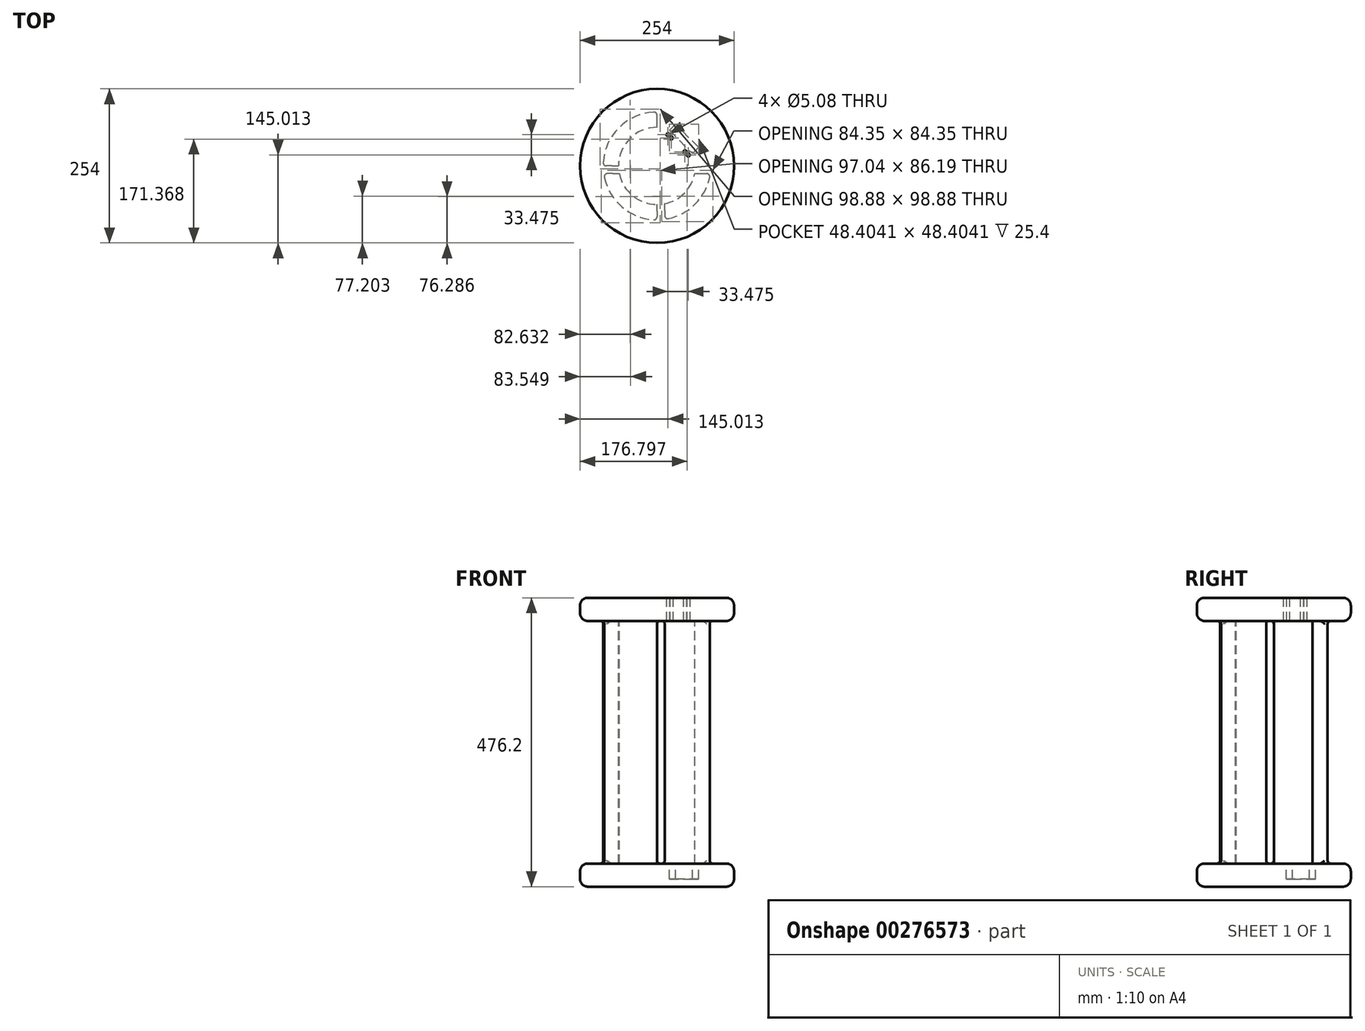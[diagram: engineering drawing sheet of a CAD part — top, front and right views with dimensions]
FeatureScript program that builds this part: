
annotation { "Feature Type Name" : "Feature", "Feature Type Description" : "" }
export const myFeature = defineFeature(function(context is Context, id is Id, definition is map)
    precondition{}
    {
        {
            var Q0;
            Q0=qCreatedBy(makeId("Top.planeOp"),FACE);
            var sketch = newSketch(context, id + "F0", { "sketchPlane" : qUnion([Q0])});
            skCircle(sketch, "E0", {"center": v(0, 0) * mm, "radius": 127 * mm});
            skSolve(sketch);
        }
        {
            var Q0;
            Q0 = qSketchRegion(id + "F0", true);
            extrude(context, id + "F1", {"entities" : qUnion([Q0]), "depth" : 38.1 * mm});
        }
        {
            var Q0;
            Q0=qCreatedBy(makeId("Front.planeOp"),FACE);
            var sketch = newSketch(context, id + "F2", { "sketchPlane" : qUnion([Q0])});
            skLineSegment(sketch, "E1.bottom", {"start": v(0, 0) * mm, "end": v(88.9, 0) * mm});
            skLineSegment(sketch, "E1.top", {"start": v(0, -400) * mm, "end": v(88.9, -400) * mm});
            skLineSegment(sketch, "E1.left", {"start": v(0, 0) * mm, "end": v(0, -400) * mm});
            skLineSegment(sketch, "E1.right", {"start": v(88.9, 0) * mm, "end": v(88.9, -400) * mm});
            skLineSegment(sketch, "E2", {"start": v(88.9, -200) * mm, "end": v(0, -200) * mm, "construction": true});
            skLineSegment(sketch, "E3", {"start": v(0, 0) * mm, "end": v(0, -87.78) * mm, "construction": true});
            skSolve(sketch);
        }
        {
            var Q0;
            Q0=makeQuery(id+"F2.imprint","IMPRINT",FACE,{"disambiguationData":[TD([[makeQuery(id+"F2.imprint","IMPRINT",EDGE,{"derivedFrom":sQuery(id+"F2.wireOp",EDGE,"E1.bottom")}),-1.0]])]});
            var Q1;
            Q1=sQuery(id+"F2.wireOp",EDGE,"E1.left");
            revolve(context, id + "F3", {"operationType" : NewBodyOperationType.ADD, "entities" : qUnion([Q0]), "axis" : qUnion([Q1]), "revolveType" : RevolveType.ONE_DIRECTION, "angle" : 278 * degree});
        }
        {
            var Q0;
            Q0=qCreatedBy(makeId("Front.planeOp"),FACE);
            var sketch = newSketch(context, id + "F4", { "sketchPlane" : qUnion([Q0])});
            skLineSegment(sketch, "E4.bottom", {"start": v(0, -400) * mm, "end": v(127, -400) * mm});
            skLineSegment(sketch, "E4.top", {"start": v(0, -438.1) * mm, "end": v(127, -438.1) * mm});
            skLineSegment(sketch, "E4.left", {"start": v(0, -400) * mm, "end": v(0, -438.1) * mm});
            skLineSegment(sketch, "E4.right", {"start": v(127, -400) * mm, "end": v(127, -438.1) * mm});
            skSolve(sketch);
        }
        {
            var Q0;
            Q0 = qSketchRegion(id + "F4", true);
            var Q1;
            Q1=makeQuery(id+"F3.opRevolve","SWEPT_FACE",FACE,{"disambiguationData":[OSD([sQuery(id+"F2.wireOp",EDGE,"E1.right")])]});
            revolve(context, id + "F5", {"operationType" : NewBodyOperationType.ADD, "entities" : qUnion([Q0]), "axis" : qUnion([Q1]), "revolveType" : RevolveType.FULL});
        }
        {
            var Q0;
            Q0=qCreatedBy(makeId("Front.planeOp"),FACE);
            var sketch = newSketch(context, id + "F6", { "sketchPlane" : qUnion([Q0])});
            skLineSegment(sketch, "E5.bottom", {"start": v(0, 0) * mm, "end": v(12.7, 0) * mm});
            skLineSegment(sketch, "E5.top", {"start": v(0, -400) * mm, "end": v(12.7, -400) * mm});
            skLineSegment(sketch, "E5.left", {"start": v(0, 0) * mm, "end": v(0, -400) * mm});
            skLineSegment(sketch, "E5.right", {"start": v(12.7, 0) * mm, "end": v(12.7, -400) * mm});
            skSolve(sketch);
        }
        {
            var Q0;
            Q0 = qSketchRegion(id + "F6", true);
            var Q1;
            Q1=makeQuery(id+"F3.opRevolve","SWEPT_FACE",FACE,{"disambiguationData":[OSD([sQuery(id+"F2.wireOp",EDGE,"E1.right")])]});
            extrude(context, id + "F7", {"entities" : qUnion([Q0]), "operationType" : NewBodyOperationType.REMOVE, "endBound" : BoundingType.SYMMETRIC, "endBoundEntityFace" : qUnion([Q1]), "depth" : 2540 * mm});
        }
        {
            var Q0;
            Q0=qCreatedBy(makeId("Right.planeOp"),FACE);
            var sketch = newSketch(context, id + "F8", { "sketchPlane" : qUnion([Q0])});
            skLineSegment(sketch, "E6.bottom", {"start": v(0, 0) * mm, "end": v(-12.7, 0) * mm});
            skLineSegment(sketch, "E6.top", {"start": v(0, -400) * mm, "end": v(-12.7, -400) * mm});
            skLineSegment(sketch, "E6.left", {"start": v(0, 0) * mm, "end": v(0, -400) * mm});
            skLineSegment(sketch, "E6.right", {"start": v(-12.7, 0) * mm, "end": v(-12.7, -400) * mm});
            skSolve(sketch);
        }
        {
            var Q0;
            Q0 = qSketchRegion(id + "F8", true);
            extrude(context, id + "F9", {"entities" : qUnion([Q0]), "operationType" : NewBodyOperationType.REMOVE, "endBound" : BoundingType.SYMMETRIC, "oppositeDirection" : true, "depth" : 2540 * mm});
        }
        {
            var Q0;
            Q0=qCreatedBy(makeId("Top.planeOp"),FACE);
            var sketch = newSketch(context, id + "F10", { "sketchPlane" : qUnion([Q0])});
            skCircle(sketch, "E7", {"center": v(0, 0) * mm, "radius": 63.5 * mm});
            skSolve(sketch);
        }
        {
            var Q0;
            Q0 = qSketchRegion(id + "F10", true);
            extrude(context, id + "F11", {"entities" : qUnion([Q0]), "operationType" : NewBodyOperationType.REMOVE, "oppositeDirection" : true, "depth" : 400 * mm});
        }
        {
            var Q0;
            Q0=makeQuery(id+"F1.opExtrude","SWEPT_FACE",FACE,{"disambiguationData":[OSD([sQuery(id+"F0.wireOp",EDGE,"E0")])]});
            fillet(context, id + "F12", {"entities" : qUnion([Q0]), "radius" : 12.7 * mm, "tangentPropagation" : true, "allowEdgeOverflow" : false});
        }
        {
            var Q0;
            Q0=makeQuery(id+"F5.opRevolve","SWEPT_FACE",FACE,{"disambiguationData":[OSD([sQuery(id+"F4.wireOp",EDGE,"E4.right")])]});
            fillet(context, id + "F13", {"entities" : qUnion([Q0]), "radius" : 12.7 * mm, "tangentPropagation" : true, "allowEdgeOverflow" : false});
        }
        {
            var Q0;
            {var subQ4=makeQuery(id+"F7.opExtrude","SWEPT_FACE",FACE,{"disambiguationData":[OSD([sQuery(id+"F6.wireOp",EDGE,"E5.right")])]});Q0=makeQuery(id+"F9.boolean.opBoolean","SPLIT",FACE,{"disambiguationData":[TD([makeQuery(id+"F9.opExtrude","SWEPT_FACE",FACE,{"disambiguationData":[OSD([sQuery(id+"F8.wireOp",EDGE,"E6.right")])]})])],"derivedFrom":makeQuery(id+"F7.boolean.opBoolean","SPLIT",FACE,{"disambiguationData":[TD([subQ4])],"derivedFrom":makeQuery(id+"F3.opRevolve","SWEPT_FACE",FACE,{"disambiguationData":[OSD([sQuery(id+"F2.wireOp",EDGE,"E1.right")])]})})});}
            var Q1;
            {var subQ4=makeQuery(id+"F7.opExtrude","SWEPT_FACE",FACE,{"disambiguationData":[OSD([sQuery(id+"F6.wireOp",EDGE,"E5.right")])]});Q1=makeQuery(id+"F9.boolean.opBoolean","SPLIT",FACE,{"disambiguationData":[TD([makeQuery(id+"F9.opExtrude","SWEPT_FACE",FACE,{"disambiguationData":[OSD([sQuery(id+"F8.wireOp",EDGE,"E6.left")])]})])],"derivedFrom":makeQuery(id+"F7.boolean.opBoolean","SPLIT",FACE,{"disambiguationData":[TD([subQ4])],"derivedFrom":makeQuery(id+"F3.opRevolve","SWEPT_FACE",FACE,{"disambiguationData":[OSD([sQuery(id+"F2.wireOp",EDGE,"E1.right")])]})})});}
            var Q2;
            {var subQ4=makeQuery(id+"F7.opExtrude","SWEPT_FACE",FACE,{"disambiguationData":[OSD([sQuery(id+"F6.wireOp",EDGE,"E5.left")])]});Q2=makeQuery(id+"F9.boolean.opBoolean","SPLIT",FACE,{"disambiguationData":[TD([makeQuery(id+"F9.opExtrude","SWEPT_FACE",FACE,{"disambiguationData":[OSD([sQuery(id+"F8.wireOp",EDGE,"E6.right")])]})])],"derivedFrom":makeQuery(id+"F7.boolean.opBoolean","SPLIT",FACE,{"disambiguationData":[TD([subQ4])],"derivedFrom":makeQuery(id+"F3.opRevolve","SWEPT_FACE",FACE,{"disambiguationData":[OSD([sQuery(id+"F2.wireOp",EDGE,"E1.right")])]})})});}
            var Q3;
            {var subQ4=makeQuery(id+"F7.opExtrude","SWEPT_FACE",FACE,{"disambiguationData":[OSD([sQuery(id+"F6.wireOp",EDGE,"E5.left")])]});Q3=makeQuery(id+"F9.boolean.opBoolean","SPLIT",FACE,{"disambiguationData":[TD([makeQuery(id+"F9.opExtrude","SWEPT_FACE",FACE,{"disambiguationData":[OSD([sQuery(id+"F8.wireOp",EDGE,"E6.left")])]})])],"derivedFrom":makeQuery(id+"F7.boolean.opBoolean","SPLIT",FACE,{"disambiguationData":[TD([subQ4])],"derivedFrom":makeQuery(id+"F3.opRevolve","SWEPT_FACE",FACE,{"disambiguationData":[OSD([sQuery(id+"F2.wireOp",EDGE,"E1.right")])]})})});}
            fillet(context, id + "F14", {"entities" : qUnion([Q0, Q1, Q2, Q3]), "radius" : 5.08 * mm, "tangentPropagation" : true, "allowEdgeOverflow" : false});
        }
        {
            var Q0;
            Q0=makeQuery(id+"F11.boolean.opBoolean","MERGE",FACE,{"derivedFrom":[makeQuery(id+"F9.boolean.opBoolean","MERGE",FACE,{"derivedFrom":[makeQuery(id+"F7.boolean.opBoolean","MERGE",FACE,{"derivedFrom":[makeQuery(id+"F5.opRevolve","SWEPT_FACE",FACE,{"disambiguationData":[OSD([sQuery(id+"F4.wireOp",EDGE,"E4.bottom")])]}),makeQuery(id+"F7.opExtrude","SWEPT_FACE",FACE,{"disambiguationData":[OSD([sQuery(id+"F6.wireOp",EDGE,"E5.top")])]})]}),makeQuery(id+"F9.opExtrude","SWEPT_FACE",FACE,{"disambiguationData":[OSD([sQuery(id+"F8.wireOp",EDGE,"E6.top")])]})]}),makeQuery(id+"F11.opExtrude","CAP_FACE",FACE,{"disambiguationData":[OSD([sQuery(id+"F10.wireOp",EDGE,"E7")])],"isStart":false})]});
            var sketch = newSketch(context, id + "F15", { "sketchPlane" : qUnion([Q0])});
            skLineSegment(sketch, "E8", {"start": v(20.32, 58.42) * mm, "end": v(58.42, 20.32) * mm});
            skLineSegment(sketch, "E9", {"start": v(20.32, 20.32) * mm, "end": v(130.3, 20.32) * mm});
            skLineSegment(sketch, "E10", {"start": v(20.32, 20.32) * mm, "end": v(20.32, 155.8) * mm});
            skLineSegment(sketch, "E11", {"start": v(153.97, -113.33) * mm, "end": v(-120.96, 161.6) * mm, "construction": true});
            skLineSegment(sketch, "E12", {"start": v(58.42, 20.32) * mm, "end": v(68.72, 30.62) * mm});
            skLineSegment(sketch, "E13", {"start": v(68.72, 30.62) * mm, "end": v(30.62, 68.72) * mm});
            skLineSegment(sketch, "E14", {"start": v(30.62, 68.72) * mm, "end": v(20.32, 58.42) * mm});
            skSolve(sketch);
        }
        {
            var Q0;
            Q0=makeQuery(id+"F15.imprint","IMPRINT",FACE,{"disambiguationData":[TD([[makeQuery(id+"F15.imprint","IMPRINT",EDGE,{"derivedFrom":sQuery(id+"F15.wireOp",EDGE,"E8")}),1.0]])]});
            extrude(context, id + "F16", {"entities" : qUnion([Q0]), "operationType" : NewBodyOperationType.REMOVE, "oppositeDirection" : true, "depth" : 25.4 * mm});
        }
        {
            var Q0;
            Q0=makeQuery(id+"F11.boolean.opBoolean","MERGE",FACE,{"derivedFrom":[makeQuery(id+"F9.boolean.opBoolean","MERGE",FACE,{"derivedFrom":[makeQuery(id+"F7.boolean.opBoolean","MERGE",FACE,{"derivedFrom":[makeQuery(id+"F1.opExtrude","CAP_FACE",FACE,{"disambiguationData":[OSD([sQuery(id+"F0.wireOp",EDGE,"E0")])],"isStart":true}),makeQuery(id+"F7.opExtrude","SWEPT_FACE",FACE,{"disambiguationData":[OSD([sQuery(id+"F6.wireOp",EDGE,"E5.bottom")])]})]}),makeQuery(id+"F9.opExtrude","SWEPT_FACE",FACE,{"disambiguationData":[OSD([sQuery(id+"F8.wireOp",EDGE,"E6.bottom")])]})]}),makeQuery(id+"F11.opExtrude","CAP_FACE",FACE,{"disambiguationData":[OSD([sQuery(id+"F10.wireOp",EDGE,"E7")])],"isStart":true})]});
            var sketch = newSketch(context, id + "F17", { "sketchPlane" : qUnion([Q0])});
            skCircle(sketch, "E15", {"center": v(23.4, -46.1) * mm, "radius": 2.54 * mm});
            skCircle(sketch, "E16", {"center": v(46.1, -23.4) * mm, "radius": 2.54 * mm});
            skLineSegment(sketch, "E17", {"start": v(0, 0) * mm, "end": v(5.08, -375.83) * mm});
            skPoint(sketch, "E18.endSnap0", {"position": v(72.48, 7.62) * mm});
            skLineSegment(sketch, "E19", {"start": v(0, 0) * mm, "end": v(375.78, 7.62) * mm});
            skLineSegment(sketch, "E20", {"start": v(0.93, -68.57) * mm, "end": v(70.94, 1.44) * mm});
            skCircle(sketch, "E21", {"center": v(18.01, -51.49) * mm, "radius": 2.54 * mm});
            skCircle(sketch, "E22", {"center": v(51.49, -18.01) * mm, "radius": 2.54 * mm});
            skSolve(sketch);
        }
        {
            var Q0;
            {var subQ0=sQuery(id+"F17.wireOp",EDGE,"E20");var subQ1=sQuery(id+"F17.wireOp",EDGE,"E15");var subQ2=makeQuery(id+"F17.imprint","INTERSECT",VERTEX,{"disambiguationData":[OD(0.0)],"derivedFrom":[subQ1,subQ0]});Q0=makeQuery(id+"F17.imprint","IMPRINT",FACE,{"disambiguationData":[TD([[makeQuery(id+"F17.imprint","IMPRINT",EDGE,{"disambiguationData":[TD([[subQ2,1.0]])],"derivedFrom":subQ1}),1.0]])]});}
            var Q1;
            {var subQ0=sQuery(id+"F17.wireOp",EDGE,"E20");var subQ1=sQuery(id+"F17.wireOp",EDGE,"E15");var subQ2=makeQuery(id+"F17.imprint","INTERSECT",VERTEX,{"disambiguationData":[OD(0.0)],"derivedFrom":[subQ1,subQ0]});Q1=makeQuery(id+"F17.imprint","IMPRINT",FACE,{"disambiguationData":[TD([[makeQuery(id+"F17.imprint","IMPRINT",EDGE,{"disambiguationData":[TD([[subQ2,-1.0]])],"derivedFrom":subQ1}),1.0]])]});}
            var Q2;
            {var subQ0=sQuery(id+"F17.wireOp",EDGE,"E20");var subQ1=sQuery(id+"F17.wireOp",EDGE,"E16");var subQ2=makeQuery(id+"F17.imprint","INTERSECT",VERTEX,{"disambiguationData":[OD(0.0)],"derivedFrom":[subQ1,subQ0]});Q2=makeQuery(id+"F17.imprint","IMPRINT",FACE,{"disambiguationData":[TD([[makeQuery(id+"F17.imprint","IMPRINT",EDGE,{"disambiguationData":[TD([[subQ2,1.0]])],"derivedFrom":subQ1}),1.0]])]});}
            var Q3;
            {var subQ0=sQuery(id+"F17.wireOp",EDGE,"E20");var subQ1=sQuery(id+"F17.wireOp",EDGE,"E16");var subQ2=makeQuery(id+"F17.imprint","INTERSECT",VERTEX,{"disambiguationData":[OD(0.0)],"derivedFrom":[subQ1,subQ0]});Q3=makeQuery(id+"F17.imprint","IMPRINT",FACE,{"disambiguationData":[TD([[makeQuery(id+"F17.imprint","IMPRINT",EDGE,{"disambiguationData":[TD([[subQ2,-1.0]])],"derivedFrom":subQ1}),1.0]])]});}
            extrude(context, id + "F18", {"entities" : qUnion([Q0, Q1, Q2, Q3]), "operationType" : NewBodyOperationType.REMOVE, "endBound" : BoundingType.THROUGH_ALL, "oppositeDirection" : true, "depth" : 30.48 * mm});
        }
        {
            var Q0;
            {var subQ0=sQuery(id+"F17.wireOp",EDGE,"E21");var subQ1=sQuery(id+"F17.wireOp",EDGE,"E20");var subQ2=makeQuery(id+"F17.imprint","INTERSECT",VERTEX,{"disambiguationData":[OD(0.0)],"derivedFrom":[subQ1,subQ0]});Q0=makeQuery(id+"F17.imprint","IMPRINT",FACE,{"disambiguationData":[TD([[makeQuery(id+"F17.imprint","IMPRINT",EDGE,{"disambiguationData":[TD([[subQ2,-1.0]])],"derivedFrom":subQ1}),-1.0]])]});}
            var Q1;
            {var subQ0=sQuery(id+"F17.wireOp",EDGE,"E21");var subQ1=sQuery(id+"F17.wireOp",EDGE,"E20");var subQ2=makeQuery(id+"F17.imprint","INTERSECT",VERTEX,{"disambiguationData":[OD(0.0)],"derivedFrom":[subQ1,subQ0]});Q1=makeQuery(id+"F17.imprint","IMPRINT",FACE,{"disambiguationData":[TD([[makeQuery(id+"F17.imprint","IMPRINT",EDGE,{"disambiguationData":[TD([[subQ2,-1.0]])],"derivedFrom":subQ1}),1.0]])]});}
            var Q2;
            {var subQ0=sQuery(id+"F17.wireOp",EDGE,"E22");var subQ1=sQuery(id+"F17.wireOp",EDGE,"E20");var subQ2=makeQuery(id+"F17.imprint","INTERSECT",VERTEX,{"disambiguationData":[OD(0.0)],"derivedFrom":[subQ1,subQ0]});Q2=makeQuery(id+"F17.imprint","IMPRINT",FACE,{"disambiguationData":[TD([[makeQuery(id+"F17.imprint","IMPRINT",EDGE,{"disambiguationData":[TD([[subQ2,-1.0]])],"derivedFrom":subQ1}),-1.0]])]});}
            var Q3;
            {var subQ0=sQuery(id+"F17.wireOp",EDGE,"E22");var subQ1=sQuery(id+"F17.wireOp",EDGE,"E20");var subQ2=makeQuery(id+"F17.imprint","INTERSECT",VERTEX,{"disambiguationData":[OD(0.0)],"derivedFrom":[subQ1,subQ0]});Q3=makeQuery(id+"F17.imprint","IMPRINT",FACE,{"disambiguationData":[TD([[makeQuery(id+"F17.imprint","IMPRINT",EDGE,{"disambiguationData":[TD([[subQ2,-1.0]])],"derivedFrom":subQ1}),1.0]])]});}
            extrude(context, id + "F19", {"entities" : qUnion([Q0, Q1, Q2, Q3]), "operationType" : NewBodyOperationType.REMOVE, "endBound" : BoundingType.THROUGH_ALL, "oppositeDirection" : true, "depth" : 25.4 * mm});
        }
    });
